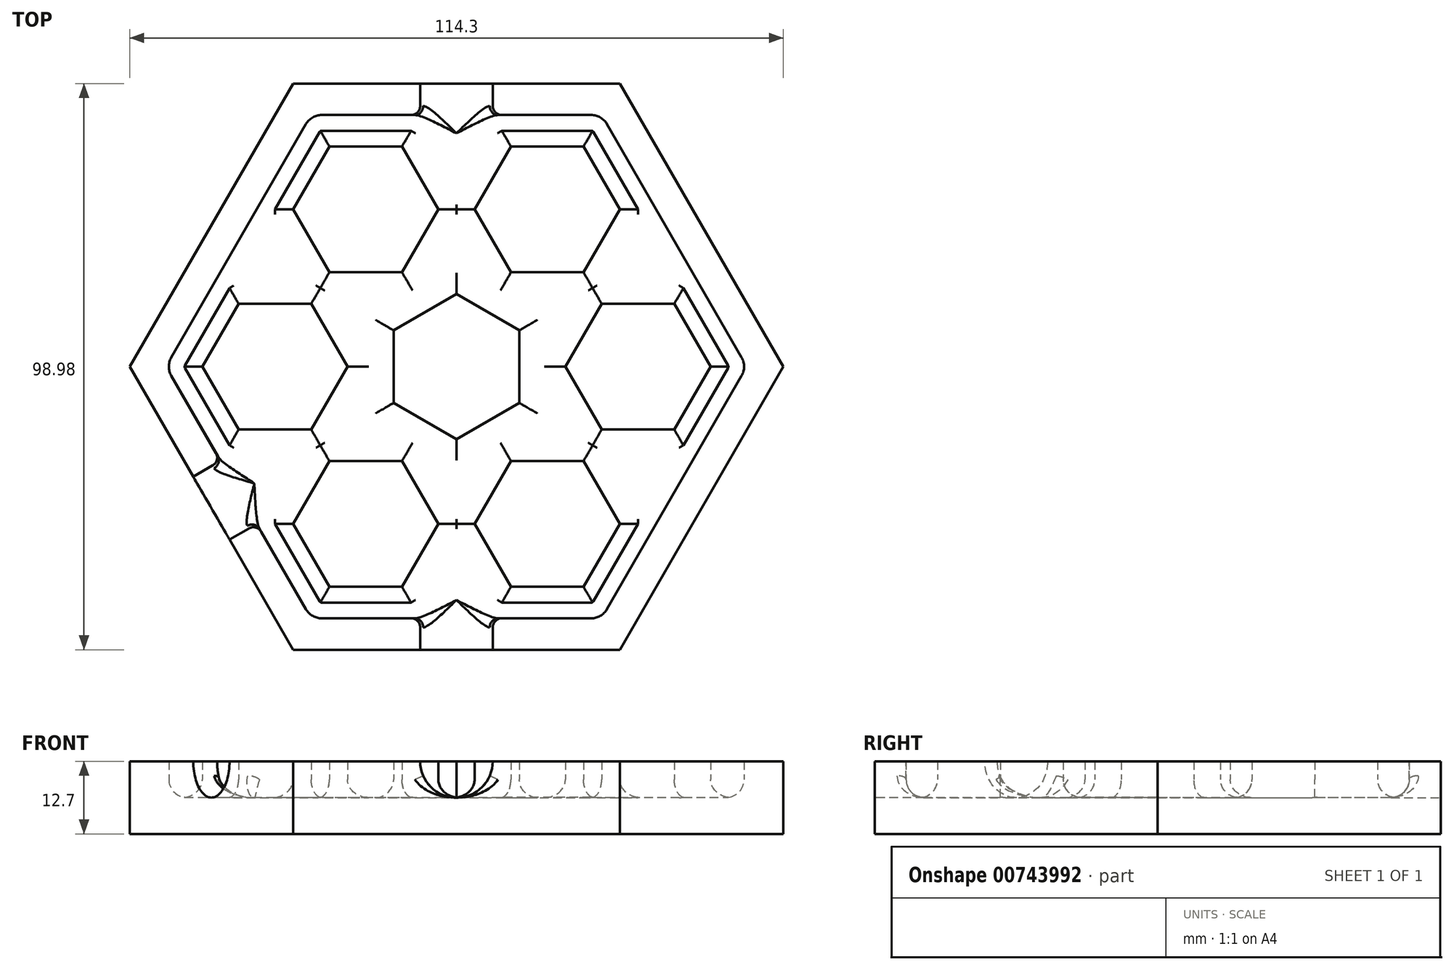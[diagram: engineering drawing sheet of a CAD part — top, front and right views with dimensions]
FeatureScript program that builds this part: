
annotation { "Feature Type Name" : "Feature", "Feature Type Description" : "" }
export const myFeature = defineFeature(function(context is Context, id is Id, definition is map)
    precondition{}
    {
        {
            var Q0;
            Q0=qCreatedBy(makeId("Top.planeOp"),FACE);
            var sketch = newSketch(context, id + "F0", { "sketchPlane" : qUnion([Q0])});
            skCircle(sketch, "E0.cCircle", {"center": v(0, 0) * mm, "radius": 57.15 * mm, "construction": true});
            skLineSegment(sketch, "E0.0", {"start": v(57.15, 0) * mm, "end": v(28.58, -49.5) * mm});
            skLineSegment(sketch, "E0.1", {"start": v(28.58, -49.5) * mm, "end": v(-28.57, -49.5) * mm});
            skLineSegment(sketch, "E0.2", {"start": v(-28.57, -49.5) * mm, "end": v(-57.15, 0) * mm});
            skLineSegment(sketch, "E0.3", {"start": v(-57.15, 0) * mm, "end": v(-28.58, 49.5) * mm});
            skLineSegment(sketch, "E0.4", {"start": v(-28.58, 49.5) * mm, "end": v(28.57, 49.5) * mm});
            skLineSegment(sketch, "E0.5", {"start": v(28.57, 49.5) * mm, "end": v(57.15, 0) * mm});
            skSolve(sketch);
        }
        {
            var Q0;
            Q0 = qSketchRegion(id + "F0", true);
            extrude(context, id + "F1", {"entities" : qUnion([Q0]), "depth" : 12.7 * mm, "offsetDistance" : 25.4 * mm});
        }
        {
            var Q0;
            Q0=makeQuery(id+"F1.opExtrude","CAP_FACE",FACE,{"disambiguationData":[OSD([sQuery(id+"F0.wireOp",EDGE,"E0.0"),sQuery(id+"F0.wireOp",EDGE,"E0.1"),sQuery(id+"F0.wireOp",EDGE,"E0.2"),sQuery(id+"F0.wireOp",EDGE,"E0.3"),sQuery(id+"F0.wireOp",EDGE,"E0.4"),sQuery(id+"F0.wireOp",EDGE,"E0.5")])],"isStart":false});
            var sketch = newSketch(context, id + "F2", { "sketchPlane" : qUnion([Q0])});
            skCircle(sketch, "E1.cCircle", {"center": v(0, 0) * mm, "radius": 50.8 * mm, "construction": true});
            skLineSegment(sketch, "E1.0", {"start": v(50.8, 0) * mm, "end": v(25.4, -44) * mm});
            skLineSegment(sketch, "E1.1", {"start": v(25.4, -44) * mm, "end": v(-25.4, -44) * mm});
            skLineSegment(sketch, "E1.2", {"start": v(-25.4, -44) * mm, "end": v(-50.8, 0) * mm});
            skLineSegment(sketch, "E1.3", {"start": v(-50.8, 0) * mm, "end": v(-25.4, 44) * mm});
            skLineSegment(sketch, "E1.4", {"start": v(-25.4, 44) * mm, "end": v(25.4, 44) * mm});
            skLineSegment(sketch, "E1.5", {"start": v(25.4, 44) * mm, "end": v(50.8, 0) * mm});
            skSolve(sketch);
        }
        {
            var Q0;
            Q0 = qSketchRegion(id + "F2", true);
            extrude(context, id + "F3", {"entities" : qUnion([Q0]), "operationType" : NewBodyOperationType.REMOVE, "oppositeDirection" : true, "depth" : 6.35 * mm, "offsetDistance" : 25.4 * mm});
        }
        {
            var Q0;
            Q0=makeQuery(id+"F3.boolean.opBoolean","COPY",FACE,{"derivedFrom":makeQuery(id+"F3.opExtrude","CAP_FACE",FACE,{"disambiguationData":[OSD([sQuery(id+"F2.wireOp",EDGE,"E1.0"),sQuery(id+"F2.wireOp",EDGE,"E1.1"),sQuery(id+"F2.wireOp",EDGE,"E1.2"),sQuery(id+"F2.wireOp",EDGE,"E1.3"),sQuery(id+"F2.wireOp",EDGE,"E1.4"),sQuery(id+"F2.wireOp",EDGE,"E1.5")])],"isStart":false})});
            var sketch = newSketch(context, id + "F4", { "sketchPlane" : qUnion([Q0])});
            skCircle(sketch, "E2.cCircle", {"center": v(0, 0) * mm, "radius": 12.7 * mm, "construction": true});
            skLineSegment(sketch, "E2.0", {"start": v(11, 6.35) * mm, "end": v(11, -6.35) * mm});
            skLineSegment(sketch, "E2.1", {"start": v(11, -6.35) * mm, "end": v(0, -12.7) * mm});
            skLineSegment(sketch, "E2.2", {"start": v(0, -12.7) * mm, "end": v(-11, -6.35) * mm});
            skLineSegment(sketch, "E2.3", {"start": v(-11, -6.35) * mm, "end": v(-11, 6.35) * mm});
            skLineSegment(sketch, "E2.4", {"start": v(-11, 6.35) * mm, "end": v(0, 12.7) * mm});
            skLineSegment(sketch, "E2.5", {"start": v(0, 12.7) * mm, "end": v(11, 6.35) * mm});
            skCircle(sketch, "E3.cCircle", {"center": v(-31.75, 0) * mm, "radius": 12.7 * mm, "construction": true});
            skLineSegment(sketch, "E3.0", {"start": v(-19.05, 0) * mm, "end": v(-25.4, -11) * mm});
            skLineSegment(sketch, "E3.1", {"start": v(-25.4, -11) * mm, "end": v(-38.1, -11) * mm});
            skLineSegment(sketch, "E3.2", {"start": v(-38.1, -11) * mm, "end": v(-44.45, 0) * mm});
            skLineSegment(sketch, "E3.3", {"start": v(-44.45, 0) * mm, "end": v(-38.1, 11) * mm});
            skLineSegment(sketch, "E3.4", {"start": v(-38.1, 11) * mm, "end": v(-25.4, 11) * mm});
            skLineSegment(sketch, "E3.5", {"start": v(-25.4, 11) * mm, "end": v(-19.05, 0) * mm});
            skLineSegment(sketch, "E4.1.0", {"start": v(-22.22, -38.5) * mm, "end": v(-28.58, -27.5) * mm});
            skLineSegment(sketch, "E4.1.1", {"start": v(-28.58, -27.5) * mm, "end": v(-22.23, -16.5) * mm});
            skLineSegment(sketch, "E4.1.2", {"start": v(-9.53, -16.5) * mm, "end": v(-3.17, -27.5) * mm});
            skCircle(sketch, "E4.1.3", {"center": v(-15.88, -27.5) * mm, "radius": 12.7 * mm, "construction": true});
            skLineSegment(sketch, "E4.1.4", {"start": v(-9.52, -38.5) * mm, "end": v(-22.23, -38.5) * mm});
            skLineSegment(sketch, "E4.1.5", {"start": v(-22.23, -16.5) * mm, "end": v(-9.52, -16.5) * mm});
            skLineSegment(sketch, "E4.1.6", {"start": v(-3.17, -27.5) * mm, "end": v(-9.52, -38.5) * mm});
            skLineSegment(sketch, "E4.2.0", {"start": v(22.22, -38.5) * mm, "end": v(9.52, -38.5) * mm});
            skLineSegment(sketch, "E4.2.1", {"start": v(9.53, -38.5) * mm, "end": v(3.17, -27.5) * mm});
            skLineSegment(sketch, "E4.2.2", {"start": v(9.52, -16.5) * mm, "end": v(22.22, -16.5) * mm});
            skCircle(sketch, "E4.2.3", {"center": v(15.87, -27.5) * mm, "radius": 12.7 * mm, "construction": true});
            skLineSegment(sketch, "E4.2.4", {"start": v(28.57, -27.5) * mm, "end": v(22.22, -38.5) * mm});
            skLineSegment(sketch, "E4.2.5", {"start": v(3.17, -27.5) * mm, "end": v(9.52, -16.5) * mm});
            skLineSegment(sketch, "E4.2.6", {"start": v(22.22, -16.5) * mm, "end": v(28.58, -27.5) * mm});
            skLineSegment(sketch, "E4.3.0", {"start": v(44.45, 0) * mm, "end": v(38.1, -11) * mm});
            skLineSegment(sketch, "E4.3.1", {"start": v(38.1, -11) * mm, "end": v(25.4, -11) * mm});
            skLineSegment(sketch, "E4.3.2", {"start": v(19.05, 0) * mm, "end": v(25.4, 11) * mm});
            skCircle(sketch, "E4.3.3", {"center": v(31.75, 0) * mm, "radius": 12.7 * mm, "construction": true});
            skLineSegment(sketch, "E4.3.4", {"start": v(38.1, 11) * mm, "end": v(44.45, 0) * mm});
            skLineSegment(sketch, "E4.3.5", {"start": v(25.4, -11) * mm, "end": v(19.05, 0) * mm});
            skLineSegment(sketch, "E4.3.6", {"start": v(25.4, 11) * mm, "end": v(38.1, 11) * mm});
            skLineSegment(sketch, "E4.4.0", {"start": v(22.23, 38.5) * mm, "end": v(28.58, 27.5) * mm});
            skLineSegment(sketch, "E4.4.1", {"start": v(28.58, 27.5) * mm, "end": v(22.23, 16.5) * mm});
            skLineSegment(sketch, "E4.4.2", {"start": v(9.53, 16.5) * mm, "end": v(3.18, 27.5) * mm});
            skCircle(sketch, "E4.4.3", {"center": v(15.88, 27.5) * mm, "radius": 12.7 * mm, "construction": true});
            skLineSegment(sketch, "E4.4.4", {"start": v(9.53, 38.5) * mm, "end": v(22.23, 38.5) * mm});
            skLineSegment(sketch, "E4.4.5", {"start": v(22.23, 16.5) * mm, "end": v(9.53, 16.5) * mm});
            skLineSegment(sketch, "E4.4.6", {"start": v(3.18, 27.5) * mm, "end": v(9.53, 38.5) * mm});
            skLineSegment(sketch, "E4.5.0", {"start": v(-22.23, 38.5) * mm, "end": v(-9.53, 38.5) * mm});
            skLineSegment(sketch, "E4.5.1", {"start": v(-9.53, 38.5) * mm, "end": v(-3.17, 27.5) * mm});
            skLineSegment(sketch, "E4.5.2", {"start": v(-9.53, 16.5) * mm, "end": v(-22.23, 16.5) * mm});
            skCircle(sketch, "E4.5.3", {"center": v(-15.88, 27.5) * mm, "radius": 12.7 * mm, "construction": true});
            skLineSegment(sketch, "E4.5.4", {"start": v(-28.58, 27.5) * mm, "end": v(-22.23, 38.5) * mm});
            skLineSegment(sketch, "E4.5.5", {"start": v(-3.18, 27.5) * mm, "end": v(-9.52, 16.5) * mm});
            skLineSegment(sketch, "E4.5.6", {"start": v(-22.23, 16.5) * mm, "end": v(-28.58, 27.5) * mm});
            skSolve(sketch);
        }
        {
            var Q0;
            Q0=makeQuery(id+"F4.imprint","IMPRINT",FACE,{"disambiguationData":[TD([[makeQuery(id+"F4.imprint","IMPRINT",EDGE,{"derivedFrom":sQuery(id+"F4.wireOp",EDGE,"E2.0")}),-1.0]])]});
            var Q1;
            Q1=makeQuery(id+"F4.imprint","IMPRINT",FACE,{"disambiguationData":[TD([[makeQuery(id+"F4.imprint","IMPRINT",EDGE,{"derivedFrom":sQuery(id+"F4.wireOp",EDGE,"E3.0")}),-1.0]])]});
            var Q2;
            Q2=makeQuery(id+"F4.imprint","IMPRINT",FACE,{"disambiguationData":[TD([[makeQuery(id+"F4.imprint","IMPRINT",EDGE,{"derivedFrom":sQuery(id+"F4.wireOp",EDGE,"62706c15-d6fb-47fe-982e-cb8f6181b1630.MirrorCS")}),1.0]])]});
            var Q3;
            Q3=makeQuery(id+"F4.imprint","IMPRINT",FACE,{"disambiguationData":[TD([[makeQuery(id+"F4.imprint","IMPRINT",EDGE,{"derivedFrom":sQuery(id+"F4.wireOp",EDGE,"7dd4fdef-c9f0-41de-a04b-6018560dac9b0.MirrorCS")}),-1.0]])]});
            var Q4;
            Q4=makeQuery(id+"F4.imprint","IMPRINT",FACE,{"disambiguationData":[TD([[makeQuery(id+"F4.imprint","IMPRINT",EDGE,{"derivedFrom":sQuery(id+"F4.wireOp",EDGE,"95675f3a-5a52-45f3-856c-d9ed02f110fc0.MirrorCS")}),1.0]])]});
            var Q5;
            Q5=makeQuery(id+"F4.imprint","IMPRINT",FACE,{"disambiguationData":[TD([[makeQuery(id+"F4.imprint","IMPRINT",EDGE,{"derivedFrom":sQuery(id+"F4.wireOp",EDGE,"6a58c16c-11e0-433a-be39-18fcc79903730.MirrorCS")}),-1.0]])]});
            var Q6;
            Q6=makeQuery(id+"F4.imprint","IMPRINT",FACE,{"disambiguationData":[TD([[makeQuery(id+"F4.imprint","IMPRINT",EDGE,{"derivedFrom":sQuery(id+"F4.wireOp",EDGE,"dc3af11b-10a0-4214-bbff-e31a450369f80.MirrorCS")}),1.0]])]});
            var Q7;
            Q7=makeQuery(id+"F4.imprint","IMPRINT",FACE,{"disambiguationData":[TD([[makeQuery(id+"F4.imprint","IMPRINT",EDGE,{"derivedFrom":sQuery(id+"F4.wireOp",EDGE,"E4.5.0")}),-1.0]])]});
            var Q8;
            Q8=makeQuery(id+"F4.imprint","IMPRINT",FACE,{"disambiguationData":[TD([[makeQuery(id+"F4.imprint","IMPRINT",EDGE,{"derivedFrom":sQuery(id+"F4.wireOp",EDGE,"E4.4.0")}),-1.0]])]});
            var Q9;
            Q9=makeQuery(id+"F4.imprint","IMPRINT",FACE,{"disambiguationData":[TD([[makeQuery(id+"F4.imprint","IMPRINT",EDGE,{"derivedFrom":sQuery(id+"F4.wireOp",EDGE,"E4.3.0")}),-1.0]])]});
            var Q10;
            Q10=makeQuery(id+"F4.imprint","IMPRINT",FACE,{"disambiguationData":[TD([[makeQuery(id+"F4.imprint","IMPRINT",EDGE,{"derivedFrom":sQuery(id+"F4.wireOp",EDGE,"E4.2.0")}),-1.0]])]});
            var Q11;
            Q11=makeQuery(id+"F4.imprint","IMPRINT",FACE,{"disambiguationData":[TD([[makeQuery(id+"F4.imprint","IMPRINT",EDGE,{"derivedFrom":sQuery(id+"F4.wireOp",EDGE,"E4.1.0")}),-1.0]])]});
            extrude(context, id + "F5", {"entities" : qUnion([Q0, Q1, Q2, Q3, Q4, Q5, Q6, Q7, Q8, Q9, Q10, Q11]), "operationType" : NewBodyOperationType.ADD, "depth" : 6.35 * mm, "offsetDistance" : 25.4 * mm});
        }
        {
            var Q0;
            Q0=makeQuery(id+"F3.boolean.opBoolean","COPY",EDGE,{"derivedFrom":makeQuery(id+"F3.opExtrude","CAP_EDGE",EDGE,{"disambiguationData":[OSD([sQuery(id+"F2.wireOp",EDGE,"E1.4")])],"isStart":false})});
            var Q1;
            Q1=makeQuery(id+"F3.boolean.opBoolean","COPY",EDGE,{"derivedFrom":makeQuery(id+"F3.opExtrude","CAP_EDGE",EDGE,{"disambiguationData":[OSD([sQuery(id+"F2.wireOp",EDGE,"E1.5")])],"isStart":false})});
            var Q2;
            Q2=makeQuery(id+"F3.boolean.opBoolean","COPY",EDGE,{"derivedFrom":makeQuery(id+"F3.opExtrude","CAP_EDGE",EDGE,{"disambiguationData":[OSD([sQuery(id+"F2.wireOp",EDGE,"E1.0")])],"isStart":false})});
            var Q3;
            Q3=makeQuery(id+"F3.boolean.opBoolean","COPY",EDGE,{"derivedFrom":makeQuery(id+"F3.opExtrude","CAP_EDGE",EDGE,{"disambiguationData":[OSD([sQuery(id+"F2.wireOp",EDGE,"E1.1")])],"isStart":false})});
            var Q4;
            Q4=makeQuery(id+"F3.boolean.opBoolean","COPY",EDGE,{"derivedFrom":makeQuery(id+"F3.opExtrude","CAP_EDGE",EDGE,{"disambiguationData":[OSD([sQuery(id+"F2.wireOp",EDGE,"E1.2")])],"isStart":false})});
            var Q5;
            Q5=makeQuery(id+"F3.boolean.opBoolean","COPY",EDGE,{"derivedFrom":makeQuery(id+"F3.opExtrude","CAP_EDGE",EDGE,{"disambiguationData":[OSD([sQuery(id+"F2.wireOp",EDGE,"E1.3")])],"isStart":false})});
            var Q6;
            Q6=makeQuery(id+"F3.boolean.opBoolean","COPY",EDGE,{"derivedFrom":makeQuery(id+"F3.opExtrude","SWEPT_EDGE",EDGE,{"disambiguationData":[OSD([sQuery(id+"F2.wireOp",EDGE,"E1.2"),sQuery(id+"F2.wireOp",EDGE,"E1.3")])]})});
            var Q7;
            Q7=makeQuery(id+"F3.boolean.opBoolean","COPY",EDGE,{"derivedFrom":makeQuery(id+"F3.opExtrude","SWEPT_EDGE",EDGE,{"disambiguationData":[OSD([sQuery(id+"F2.wireOp",EDGE,"E1.1"),sQuery(id+"F2.wireOp",EDGE,"E1.2")])]})});
            var Q8;
            Q8=makeQuery(id+"F3.boolean.opBoolean","COPY",EDGE,{"derivedFrom":makeQuery(id+"F3.opExtrude","SWEPT_EDGE",EDGE,{"disambiguationData":[OSD([sQuery(id+"F2.wireOp",EDGE,"E1.0"),sQuery(id+"F2.wireOp",EDGE,"E1.1")])]})});
            var Q9;
            Q9=makeQuery(id+"F3.boolean.opBoolean","COPY",EDGE,{"derivedFrom":makeQuery(id+"F3.opExtrude","SWEPT_EDGE",EDGE,{"disambiguationData":[OSD([sQuery(id+"F2.wireOp",EDGE,"E1.0"),sQuery(id+"F2.wireOp",EDGE,"E1.5")])]})});
            var Q10;
            Q10=makeQuery(id+"F3.boolean.opBoolean","COPY",EDGE,{"derivedFrom":makeQuery(id+"F3.opExtrude","SWEPT_EDGE",EDGE,{"disambiguationData":[OSD([sQuery(id+"F2.wireOp",EDGE,"E1.4"),sQuery(id+"F2.wireOp",EDGE,"E1.5")])]})});
            var Q11;
            Q11=makeQuery(id+"F3.boolean.opBoolean","COPY",EDGE,{"derivedFrom":makeQuery(id+"F3.opExtrude","SWEPT_EDGE",EDGE,{"disambiguationData":[OSD([sQuery(id+"F2.wireOp",EDGE,"E1.3"),sQuery(id+"F2.wireOp",EDGE,"E1.4")])]})});
            var Q12;
            Q12=makeQuery(id+"F3.boolean.opBoolean","COPY",FACE,{"derivedFrom":makeQuery(id+"F3.opExtrude","CAP_FACE",FACE,{"disambiguationData":[OSD([sQuery(id+"F2.wireOp",EDGE,"E1.0"),sQuery(id+"F2.wireOp",EDGE,"E1.1"),sQuery(id+"F2.wireOp",EDGE,"E1.2"),sQuery(id+"F2.wireOp",EDGE,"E1.3"),sQuery(id+"F2.wireOp",EDGE,"E1.4"),sQuery(id+"F2.wireOp",EDGE,"E1.5")])],"isStart":false})});
            fillet(context, id + "F6", {"entities" : qUnion([Q0, Q1, Q2, Q3, Q4, Q5, Q6, Q7, Q8, Q9, Q10, Q11, Q12]), "radius" : 3.17 * mm, "tangentPropagation" : true, "allowEdgeOverflow" : false});
        }
        {
            var Q0;
            Q0=makeQuery(id+"F1.opExtrude","SWEPT_FACE",FACE,{"disambiguationData":[OSD([sQuery(id+"F0.wireOp",EDGE,"E0.2")])]});
            var sketch = newSketch(context, id + "F7", { "sketchPlane" : qUnion([Q0])});
            skCircle(sketch, "E5", {"center": v(0, 12.7) * mm, "radius": 6.35 * mm});
            skSolve(sketch);
        }
        {
            var Q0;
            Q0=makeQuery(id+"F1.opExtrude","SWEPT_FACE",FACE,{"disambiguationData":[OSD([sQuery(id+"F0.wireOp",EDGE,"E0.1")])]});
            var sketch = newSketch(context, id + "F8", { "sketchPlane" : qUnion([Q0])});
            skCircle(sketch, "E6", {"center": v(0, 12.7) * mm, "radius": 6.35 * mm});
            skSolve(sketch);
        }
        {
            var Q0;
            Q0=makeQuery(id+"F1.opExtrude","SWEPT_FACE",FACE,{"disambiguationData":[OSD([sQuery(id+"F0.wireOp",EDGE,"E0.4")])]});
            var sketch = newSketch(context, id + "F9", { "sketchPlane" : qUnion([Q0])});
            skCircle(sketch, "E7", {"center": v(0, 12.7) * mm, "radius": 6.35 * mm});
            skSolve(sketch);
        }
        {
            var Q0;
            Q0 = qSketchRegion(id + "F7", true);
            extrude(context, id + "F10", {"entities" : qUnion([Q0]), "operationType" : NewBodyOperationType.REMOVE, "oppositeDirection" : true, "depth" : 9.52 * mm, "offsetDistance" : 25.4 * mm});
        }
        {
            var Q0;
            Q0 = qSketchRegion(id + "F8", true);
            extrude(context, id + "F11", {"entities" : qUnion([Q0]), "operationType" : NewBodyOperationType.REMOVE, "oppositeDirection" : true, "depth" : 9.52 * mm, "offsetDistance" : 25.4 * mm});
        }
        {
            var Q0;
            Q0 = qSketchRegion(id + "F9", true);
            extrude(context, id + "F12", {"entities" : qUnion([Q0]), "operationType" : NewBodyOperationType.REMOVE, "oppositeDirection" : true, "depth" : 9.52 * mm, "offsetDistance" : 25.4 * mm});
        }
        {
            var Q0;
            Q0=makeQuery(id+"F11.boolean.opBoolean","INTERSECT",EDGE,{"disambiguationData":[OD(1.0)],"derivedFrom":[makeQuery(id+"F6.opFillet","BLEND_FACE",FACE,{"disambiguationData":[OSD([sQuery(id+"F2.wireOp",EDGE,"E1.1")]),OD(1.0)]}),makeQuery(id+"F11.opExtrude","SWEPT_FACE",FACE,{"disambiguationData":[OSD([sQuery(id+"F8.wireOp",EDGE,"E6")])]})]});
            var Q1;
            Q1=makeQuery(id+"F11.boolean.opBoolean","INTERSECT",EDGE,{"disambiguationData":[OD(0.0)],"derivedFrom":[makeQuery(id+"F6.opFillet","BLEND_FACE",FACE,{"disambiguationData":[OSD([sQuery(id+"F2.wireOp",EDGE,"E1.1")]),OD(1.0)]}),makeQuery(id+"F11.opExtrude","SWEPT_FACE",FACE,{"disambiguationData":[OSD([sQuery(id+"F8.wireOp",EDGE,"E6")])]})]});
            var Q2;
            Q2=makeQuery(id+"F10.boolean.opBoolean","INTERSECT",EDGE,{"disambiguationData":[OD(0.0)],"derivedFrom":[makeQuery(id+"F6.opFillet","BLEND_FACE",FACE,{"disambiguationData":[OSD([sQuery(id+"F2.wireOp",EDGE,"E1.2")]),OD(1.0)]}),makeQuery(id+"F10.opExtrude","SWEPT_FACE",FACE,{"disambiguationData":[OSD([sQuery(id+"F7.wireOp",EDGE,"E5")])]})]});
            var Q3;
            Q3=makeQuery(id+"F10.boolean.opBoolean","INTERSECT",EDGE,{"disambiguationData":[OD(1.0)],"derivedFrom":[makeQuery(id+"F6.opFillet","BLEND_FACE",FACE,{"disambiguationData":[OSD([sQuery(id+"F2.wireOp",EDGE,"E1.2")]),OD(1.0)]}),makeQuery(id+"F10.opExtrude","SWEPT_FACE",FACE,{"disambiguationData":[OSD([sQuery(id+"F7.wireOp",EDGE,"E5")])]})]});
            var Q4;
            Q4=makeQuery(id+"F12.boolean.opBoolean","INTERSECT",EDGE,{"disambiguationData":[OD(0.0)],"derivedFrom":[makeQuery(id+"F6.opFillet","BLEND_FACE",FACE,{"disambiguationData":[OSD([sQuery(id+"F2.wireOp",EDGE,"E1.4")]),OD(1.0)]}),makeQuery(id+"F12.opExtrude","SWEPT_FACE",FACE,{"disambiguationData":[OSD([sQuery(id+"F9.wireOp",EDGE,"E7")])]})]});
            var Q5;
            Q5=makeQuery(id+"F12.boolean.opBoolean","INTERSECT",EDGE,{"disambiguationData":[OD(1.0)],"derivedFrom":[makeQuery(id+"F6.opFillet","BLEND_FACE",FACE,{"disambiguationData":[OSD([sQuery(id+"F2.wireOp",EDGE,"E1.4")]),OD(1.0)]}),makeQuery(id+"F12.opExtrude","SWEPT_FACE",FACE,{"disambiguationData":[OSD([sQuery(id+"F9.wireOp",EDGE,"E7")])]})]});
            fillet(context, id + "F13", {"entities" : qUnion([Q0, Q1, Q2, Q3, Q4, Q5]), "radius" : 1.59 * mm, "tangentPropagation" : true, "allowEdgeOverflow" : false});
        }
    });
